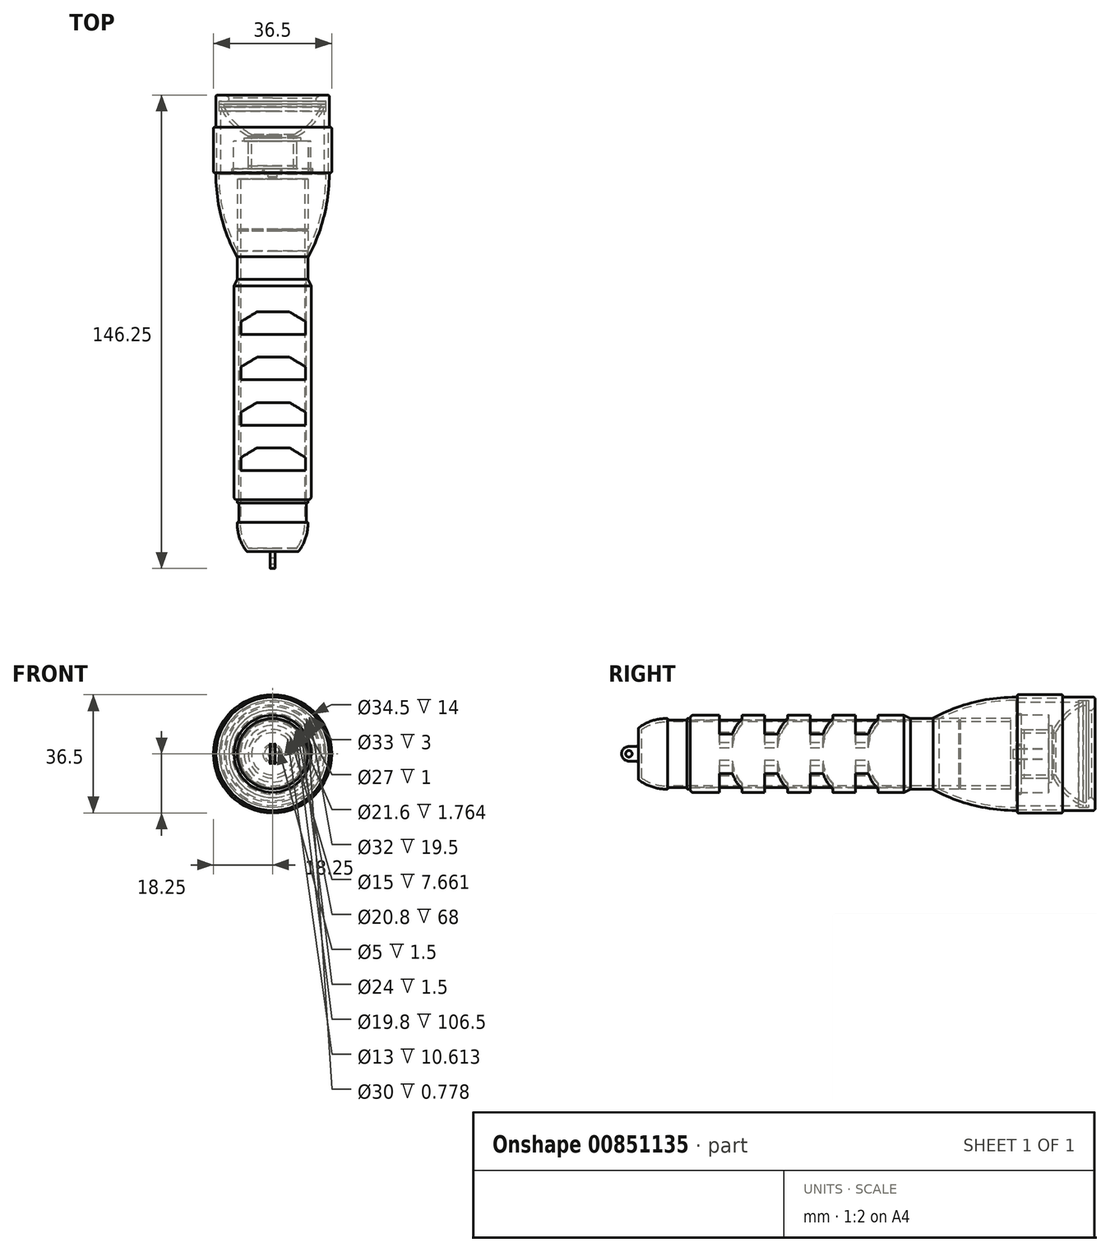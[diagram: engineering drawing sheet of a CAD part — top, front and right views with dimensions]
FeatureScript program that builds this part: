
annotation { "Feature Type Name" : "Feature", "Feature Type Description" : "" }
export const myFeature = defineFeature(function(context is Context, id is Id, definition is map)
    precondition{}
    {
        {
            var Q0;
            Q0=qCreatedBy(makeId("Right.planeOp"),FACE);
            var sketch = newSketch(context, id + "F0", { "sketchPlane" : qUnion([Q0])});
            skLineSegment(sketch, "E0", {"start": v(-10, 17.5) * mm, "end": v(0, 17.5) * mm});
            skLineSegment(sketch, "E1", {"start": v(0, 17.5) * mm, "end": v(0, 13.5) * mm});
            skLineSegment(sketch, "E2", {"start": v(0, 13.5) * mm, "end": v(-2, 13.5) * mm});
            skLineSegment(sketch, "E3", {"start": v(-2, 13.5) * mm, "end": v(-2, 16.5) * mm});
            skLineSegment(sketch, "E4", {"start": v(-2, 16.5) * mm, "end": v(-10, 16.5) * mm});
            skLineSegment(sketch, "E5", {"start": v(-10, 16.5) * mm, "end": v(-10, 17.5) * mm});
            skLineSegment(sketch, "E6", {"start": v(0, 0) * mm, "end": v(-44.18, 0) * mm, "construction": true});
            skSolve(sketch);
        }
        {
            var Q0;
            Q0 = qSketchRegion(id + "F0", true);
            var Q1;
            Q1=sQuery(id+"F0.wireOp",EDGE,"E6");
            revolve(context, id + "F1", {"surfaceOperationType" : NewSurfaceOperationType.NEW, "entities" : qUnion([Q0]), "axis" : qUnion([Q1]), "revolveType" : RevolveType.FULL});
        }
        {
            var Q0;
            Q0=makeQuery(id+"F1.opRevolve","SWEPT_EDGE",EDGE,{"disambiguationData":[OSD([sQuery(id+"F0.wireOp",EDGE,"E1"),sQuery(id+"F0.wireOp",EDGE,"E2")])]});
            chamfer(context, id + "F2", {"entities" : qUnion([Q0]), "width" : 1 * mm, "tangentPropagation" : true});
        }
        {
            var Q0;
            Q0=makeQuery(id+"F1.opRevolve","SWEPT_EDGE",EDGE,{"disambiguationData":[OSD([sQuery(id+"F0.wireOp",EDGE,"E0"),sQuery(id+"F0.wireOp",EDGE,"E1")])]});
            fillet(context, id + "F3", {"entities" : qUnion([Q0]), "radius" : .5 * mm, "tangentPropagation" : true, "allowEdgeOverflow" : false});
        }
        {
            var Q0;
            Q0=qCreatedBy(makeId("Right.planeOp"),FACE);
            var sketch = newSketch(context, id + "F4", { "sketchPlane" : qUnion([Q0])});
            skLineSegment(sketch, "E7.bottom", {"start": v(-2, 16.5) * mm, "end": v(-2.8, 16.5) * mm});
            skLineSegment(sketch, "E7.top", {"start": v(-2, 0) * mm, "end": v(-2.8, 0) * mm});
            skLineSegment(sketch, "E7.left", {"start": v(-2, 16.5) * mm, "end": v(-2, 0) * mm});
            skLineSegment(sketch, "E7.right", {"start": v(-2.8, 16.5) * mm, "end": v(-2.8, 0) * mm});
            skSolve(sketch);
        }
        {
            var Q0;
            Q0 = qSketchRegion(id + "F4", true);
            var Q1;
            Q1=sQuery(id+"F4.wireOp",EDGE,"E7.top");
            revolve(context, id + "F5", {"surfaceOperationType" : NewSurfaceOperationType.NEW, "entities" : qUnion([Q0]), "axis" : qUnion([Q1]), "revolveType" : RevolveType.FULL});
        }
        {
            var Q0;
            Q0=qCreatedBy(makeId("Right.planeOp"),FACE);
            var sketch = newSketch(context, id + "F6", { "sketchPlane" : qUnion([Q0])});
            skLineSegment(sketch, "E8", {"start": v(-22.8, 7.5) * mm, "end": v(-14.3, 7.5) * mm});
            skLineSegment(sketch, "E9", {"start": v(-22.8, 7.5) * mm, "end": v(-22.8, 6.5) * mm});
            skLineSegment(sketch, "E10", {"start": v(-22.8, 6.5) * mm, "end": v(-12.19, 6.5) * mm});
            skLineSegment(sketch, "E11", {"start": v(-3.8, 16.5) * mm, "end": v(-2.8, 16.5) * mm});
            skLineSegment(sketch, "E12", {"start": v(-2.8, 16.5) * mm, "end": v(-2.8, 15) * mm});
            skLineSegment(sketch, "E13", {"start": v(-3.8, 16.5) * mm, "end": v(-3.8, 16) * mm});
            skLineSegment(sketch, "E14", {"start": v(-3.8, 16) * mm, "end": v(2.7, 16) * mm, "construction": true});
            skArc(sketch, "E15", {"start": v(-3.8, 16) * mm, "mid": v(-9, 12.5) * mm, "end": v(-12.8, 7.5) * mm});
            skArc(sketch, "E16.0", {"start": v(-3.58, 15) * mm, "mid": v(-8.6, 11.48) * mm, "end": v(-12.19, 6.5) * mm});
            skLineSegment(sketch, "E17", {"start": v(-3.58, 15) * mm, "end": v(-2.8, 15) * mm});
            skLineSegment(sketch, "E18", {"start": v(-14.3, 7.5) * mm, "end": v(-14.3, 8.75) * mm});
            skLineSegment(sketch, "E19", {"start": v(-14.3, 8.75) * mm, "end": v(-13.3, 8.75) * mm});
            skLineSegment(sketch, "E20", {"start": v(-13.3, 8.75) * mm, "end": v(-13.3, 7.5) * mm});
            skLineSegment(sketch, "E21", {"start": v(-13.3, 7.5) * mm, "end": v(-12.8, 7.5) * mm});
            skSolve(sketch);
        }
        {
            var Q0;
            Q0 = qSketchRegion(id + "F6", true);
            var Q1;
            Q1=sQuery(id+"F0.wireOp",EDGE,"E6");
            revolve(context, id + "F7", {"surfaceOperationType" : NewSurfaceOperationType.NEW, "entities" : qUnion([Q0]), "axis" : qUnion([Q1]), "revolveType" : RevolveType.FULL});
        }
        {
            var Q0;
            Q0=qCreatedBy(makeId("Right.planeOp"),FACE);
            var sketch = newSketch(context, id + "F8", { "sketchPlane" : qUnion([Q0])});
            skLineSegment(sketch, "E22", {"start": v(-5, 16.5) * mm, "end": v(-10, 16.5) * mm});
            skLineSegment(sketch, "E23", {"start": v(-10, 16.5) * mm, "end": v(-10, 17.25) * mm});
            skLineSegment(sketch, "E24", {"start": v(-10, 17.25) * mm, "end": v(-24, 17.25) * mm});
            skLineSegment(sketch, "E25", {"start": v(-24, 17.25) * mm, "end": v(-24, 17.5) * mm});
            skLineSegment(sketch, "E26", {"start": v(-24, 17.5) * mm, "end": v(-24.5, 17.5) * mm});
            skArc(sketch, "E27", {"start": v(-24.5, 17.5) * mm, "mid": v(-37.66, 15.85) * mm, "end": v(-50, 11) * mm});
            skLineSegment(sketch, "E28", {"start": v(-5, 16.5) * mm, "end": v(-3.8, 16.5) * mm, "construction": true});
            skArc(sketch, "E29.0", {"start": v(-24.5, 16.5) * mm, "mid": v(-36.7, 15.06) * mm, "end": v(-48.24, 10.8) * mm});
            skLineSegment(sketch, "E30", {"start": v(-50, 11) * mm, "end": v(-50, 10.8) * mm});
            skLineSegment(sketch, "E31", {"start": v(-50, 10.8) * mm, "end": v(-48.24, 10.8) * mm});
            skLineSegment(sketch, "E32", {"start": v(-5, 16.5) * mm, "end": v(-5, 16) * mm});
            skLineSegment(sketch, "E33", {"start": v(-5, 16) * mm, "end": v(-24.5, 16) * mm});
            skLineSegment(sketch, "E34", {"start": v(-24.5, 16.5) * mm, "end": v(-24.5, 16) * mm});
            skSolve(sketch);
        }
        {
            var Q0;
            Q0 = qSketchRegion(id + "F8", true);
            var Q1;
            Q1=sQuery(id+"F0.wireOp",EDGE,"E6");
            revolve(context, id + "F9", {"operationType" : NewBodyOperationType.ADD, "surfaceOperationType" : NewSurfaceOperationType.NEW, "entities" : qUnion([Q0]), "axis" : qUnion([Q1]), "revolveType" : RevolveType.FULL});
        }
        {
            var Q0;
            Q0=qCreatedBy(makeId("Right.planeOp"),FACE);
            var sketch = newSketch(context, id + "F10", { "sketchPlane" : qUnion([Q0])});
            skLineSegment(sketch, "E35.bottom", {"start": v(-24, 18.25) * mm, "end": v(-10, 18.25) * mm});
            skLineSegment(sketch, "E35.top", {"start": v(-24, 17.25) * mm, "end": v(-10, 17.25) * mm});
            skLineSegment(sketch, "E35.left", {"start": v(-24, 18.25) * mm, "end": v(-24, 17.25) * mm});
            skLineSegment(sketch, "E35.right", {"start": v(-10, 18.25) * mm, "end": v(-10, 17.25) * mm});
            skSolve(sketch);
        }
        {
            var Q0;
            Q0 = qSketchRegion(id + "F10", true);
            var Q1;
            Q1=sQuery(id+"F0.wireOp",EDGE,"E6");
            revolve(context, id + "F11", {"surfaceOperationType" : NewSurfaceOperationType.NEW, "entities" : qUnion([Q0]), "axis" : qUnion([Q1]), "revolveType" : RevolveType.FULL});
        }
        {
            var Q0;
            Q0=makeQuery(id+"F11.opRevolve","SWEPT_EDGE",EDGE,{"disambiguationData":[OSD([sQuery(id+"F10.wireOp",EDGE,"E35.bottom"),sQuery(id+"F10.wireOp",EDGE,"E35.left")])]});
            var Q1;
            Q1=makeQuery(id+"F11.opRevolve","SWEPT_EDGE",EDGE,{"disambiguationData":[OSD([sQuery(id+"F10.wireOp",EDGE,"E35.bottom"),sQuery(id+"F10.wireOp",EDGE,"E35.right")])]});
            fillet(context, id + "F12", {"entities" : qUnion([Q0, Q1]), "radius" : .3 * mm, "tangentPropagation" : true, "allowEdgeOverflow" : false});
        }
        {
            var Q0;
            Q0=qCreatedBy(makeId("Right.planeOp"),FACE);
            var sketch = newSketch(context, id + "F13", { "sketchPlane" : qUnion([Q0])});
            skLineSegment(sketch, "E36", {"start": v(-41.5, 10.9) * mm, "end": v(-26, 10.9) * mm});
            skLineSegment(sketch, "E37", {"start": v(-26, 10.9) * mm, "end": v(-26, 10.4) * mm});
            skLineSegment(sketch, "E38", {"start": v(-41.5, 10.9) * mm, "end": v(-41.5, 10.4) * mm});
            skLineSegment(sketch, "E39", {"start": v(-41.5, 10.4) * mm, "end": v(-42, 10.4) * mm});
            skLineSegment(sketch, "E40", {"start": v(-42, 10.4) * mm, "end": v(-42, 10.9) * mm});
            skLineSegment(sketch, "E41", {"start": v(-42, 10.9) * mm, "end": v(-57, 10.9) * mm});
            skLineSegment(sketch, "E42", {"start": v(-57, 10.9) * mm, "end": v(-57, 10.4) * mm});
            skLineSegment(sketch, "E43", {"start": v(-125, 10.9) * mm, "end": v(-126, 10.9) * mm});
            skLineSegment(sketch, "E44", {"start": v(-126, 10.9) * mm, "end": v(-126, 10.4) * mm});
            skLineSegment(sketch, "E45", {"start": v(-235.67, 8.05) * mm, "end": v(-235.67, 10.9) * mm});
            skLineSegment(sketch, "E46", {"start": v(-141, 0) * mm, "end": v(-141, 8) * mm});
            skArc(sketch, "E47", {"start": v(-132.5, 10.9) * mm, "mid": v(-137, 10.16) * mm, "end": v(-141, 8) * mm});
            skLineSegment(sketch, "E48", {"start": v(-57, 10.4) * mm, "end": v(-125, 10.4) * mm});
            skLineSegment(sketch, "E49", {"start": v(-125, 10.4) * mm, "end": v(-125, 10.9) * mm});
            skLineSegment(sketch, "E50", {"start": v(-126, 10.4) * mm, "end": v(-132, 10.4) * mm});
            skLineSegment(sketch, "E51", {"start": v(-132, 10.4) * mm, "end": v(-132, 10.9) * mm});
            skLineSegment(sketch, "E52", {"start": v(-132, 10.9) * mm, "end": v(-132.5, 10.9) * mm});
            skLineSegment(sketch, "E53.0", {"start": v(-26, 9.9) * mm, "end": v(-132.5, 9.9) * mm});
            skLineSegment(sketch, "E54", {"start": v(-26, 9.9) * mm, "end": v(-26, 10.4) * mm});
            skArc(sketch, "E55.0", {"start": v(-132.5, 9.9) * mm, "mid": v(-136.44, 9.28) * mm, "end": v(-140, 7.5) * mm});
            skLineSegment(sketch, "E55.1", {"start": v(-140, 0) * mm, "end": v(-140, 7.5) * mm});
            skLineSegment(sketch, "E56", {"start": v(-141, 0) * mm, "end": v(-140, 0) * mm});
            skLineSegment(sketch, "E57", {"start": v(-26, 10.9) * mm, "end": v(10.32, 10.9) * mm, "construction": true});
            skLineSegment(sketch, "E58", {"start": v(0, 0) * mm, "end": v(10.28, 0) * mm});
            skLineSegment(sketch, "E59", {"start": v(-132.5, 10.9) * mm, "end": v(-141.04, 10.9) * mm, "construction": true});
            skSolve(sketch);
        }
        {
            var Q0;
            Q0=makeQuery(id+"F13.imprint","IMPRINT",FACE,{"disambiguationData":[TD([[makeQuery(id+"F13.imprint","IMPRINT",EDGE,{"derivedFrom":sQuery(id+"F13.wireOp",EDGE,"E36")}),-1.0]])]});
            var Q1;
            Q1=sQuery(id+"F13.wireOp",EDGE,"E56");
            revolve(context, id + "F14", {"surfaceOperationType" : NewSurfaceOperationType.NEW, "entities" : qUnion([Q0]), "axis" : qUnion([Q1]), "revolveType" : RevolveType.FULL});
        }
        {
            var Q0;
            Q0=qCreatedBy(makeId("Right.planeOp"),FACE);
            var sketch = newSketch(context, id + "F15", { "sketchPlane" : qUnion([Q0])});
            skLineSegment(sketch, "E60.bottom", {"start": v(-125, 10.4) * mm, "end": v(-57, 10.4) * mm});
            skLineSegment(sketch, "E60.top", {"start": v(-125, 11.9) * mm, "end": v(-57, 11.9) * mm});
            skLineSegment(sketch, "E60.left", {"start": v(-125, 10.4) * mm, "end": v(-125, 11.9) * mm});
            skLineSegment(sketch, "E60.right", {"start": v(-57, 10.4) * mm, "end": v(-57, 11.9) * mm});
            skSolve(sketch);
        }
        {
            var Q0;
            Q0 = qSketchRegion(id + "F15", true);
            var Q1;
            Q1=sQuery(id+"F0.wireOp",EDGE,"E6");
            revolve(context, id + "F16", {"surfaceOperationType" : NewSurfaceOperationType.NEW, "entities" : qUnion([Q0]), "axis" : qUnion([Q1]), "revolveType" : RevolveType.FULL});
        }
        {
            var Q0;
            Q0=qCreatedBy(makeId("Right.planeOp"),FACE);
            var sketch = newSketch(context, id + "F17", { "sketchPlane" : qUnion([Q0])});
            skCircle(sketch, "E61", {"center": v(-144, 0) * mm, "radius": 1 * mm});
            skArc(sketch, "E62", {"start": v(-144, 2.25) * mm, "mid": v(-146.25, 0) * mm, "end": v(-144, -2.25) * mm});
            skLineSegment(sketch, "E63", {"start": v(-144, 2.25) * mm, "end": v(-140.57, 2.25) * mm});
            skLineSegment(sketch, "E64", {"start": v(-140.57, 2.25) * mm, "end": v(-140.57, -2.25) * mm});
            skLineSegment(sketch, "E65", {"start": v(-140.57, -2.25) * mm, "end": v(-144, -2.25) * mm});
            skSolve(sketch);
        }
        {
            var Q0;
            Q0 = qSketchRegion(id + "F17", true);
            extrude(context, id + "F18", {"entities" : qUnion([Q0]), "operationType" : NewBodyOperationType.ADD, "endBound" : BoundingType.SYMMETRIC, "depth" : 1.5 * mm, "offsetDistance" : 25 * mm});
        }
        {
            var Q0;
            Q0=makeQuery(id+"F18.boolean.opBoolean","INTERSECT",EDGE,{"derivedFrom":[makeQuery(id+"F14.opRevolve","SWEPT_FACE",FACE,{"disambiguationData":[OSD([sQuery(id+"F13.wireOp",EDGE,"E46")])]}),makeQuery(id+"F18.opExtrude","SWEPT_FACE",FACE,{"disambiguationData":[OSD([sQuery(id+"F17.wireOp",EDGE,"E63")])]})]});
            var Q1;
            Q1=makeQuery(id+"F18.boolean.opBoolean","INTERSECT",EDGE,{"derivedFrom":[makeQuery(id+"F14.opRevolve","SWEPT_FACE",FACE,{"disambiguationData":[OSD([sQuery(id+"F13.wireOp",EDGE,"E46")])]}),makeQuery(id+"F18.opExtrude","SWEPT_FACE",FACE,{"disambiguationData":[OSD([sQuery(id+"F17.wireOp",EDGE,"E65")])]})]});
            fillet(context, id + "F19", {"entities" : qUnion([Q0, Q1]), "radius" : 1 * mm, "tangentPropagation" : true, "allowEdgeOverflow" : false});
        }
        {
            var Q0;
            Q0=makeQuery(id+"F16.opRevolve","SWEPT_EDGE",EDGE,{"disambiguationData":[OSD([sQuery(id+"F15.wireOp",EDGE,"E60.top"),sQuery(id+"F15.wireOp",EDGE,"E60.right")])]});
            chamfer(context, id + "F20", {"entities" : qUnion([Q0]), "chamferType" : ChamferType.TWO_OFFSETS, "width1" : 1 * mm, "oppositeDirection" : false, "width2" : 2 * mm, "tangentPropagation" : true});
        }
        {
            var Q0;
            Q0=makeQuery(id+"F16.opRevolve","SWEPT_EDGE",EDGE,{"disambiguationData":[OSD([sQuery(id+"F15.wireOp",EDGE,"E60.top"),sQuery(id+"F15.wireOp",EDGE,"E60.left")])]});
            fillet(context, id + "F21", {"entities" : qUnion([Q0]), "radius" : .8 * mm, "tangentPropagation" : true, "allowEdgeOverflow" : false});
        }
        {
            var Q0;
            Q0=makeQuery(id+"F14.opRevolve","SWEPT_EDGE",EDGE,{"disambiguationData":[OSD([sQuery(id+"F13.wireOp",EDGE,"E43"),sQuery(id+"F13.wireOp",EDGE,"E44")])]});
            var Q1;
            Q1=makeQuery(id+"F14.opRevolve","SWEPT_EDGE",EDGE,{"disambiguationData":[OSD([sQuery(id+"F13.wireOp",EDGE,"E51"),sQuery(id+"F13.wireOp",EDGE,"E52")])]});
            var Q2;
            Q2=makeQuery(id+"F14.opRevolve","SWEPT_EDGE",EDGE,{"disambiguationData":[OSD([sQuery(id+"F13.wireOp",EDGE,"E44"),sQuery(id+"F13.wireOp",EDGE,"E50")])]});
            var Q3;
            Q3=makeQuery(id+"F14.opRevolve","SWEPT_EDGE",EDGE,{"disambiguationData":[OSD([sQuery(id+"F13.wireOp",EDGE,"E50"),sQuery(id+"F13.wireOp",EDGE,"E51")])]});
            var Q4;
            Q4=makeQuery(id+"F18.opExtrude","CAP_EDGE",EDGE,{"disambiguationData":[OSD([sQuery(id+"F17.wireOp",EDGE,"E61")])],"isStart":false});
            var Q5;
            Q5=makeQuery(id+"F18.opExtrude","CAP_EDGE",EDGE,{"disambiguationData":[OSD([sQuery(id+"F17.wireOp",EDGE,"E63")])],"isStart":false});
            var Q6;
            Q6=makeQuery(id+"F18.opExtrude","CAP_EDGE",EDGE,{"disambiguationData":[OSD([sQuery(id+"F17.wireOp",EDGE,"E61")])],"isStart":true});
            var Q7;
            Q7=makeQuery(id+"F18.opExtrude","CAP_EDGE",EDGE,{"disambiguationData":[OSD([sQuery(id+"F17.wireOp",EDGE,"E62")])],"isStart":true});
            var Q8;
            {var subQ0=makeQuery(id+"F14.opRevolve","SWEPT_FACE",FACE,{"disambiguationData":[OSD([sQuery(id+"F13.wireOp",EDGE,"E46")])]});Q8=makeQuery(id+"F19.opFillet","BLEND_EDGE",EDGE,{"blendedFrom":[makeQuery(id+"F18.boolean.opBoolean","INTERSECT",EDGE,{"derivedFrom":[subQ0,makeQuery(id+"F18.opExtrude","SWEPT_FACE",FACE,{"disambiguationData":[OSD([sQuery(id+"F17.wireOp",EDGE,"E63")])]})]}),subQ0],"blendedInto":[subQ0]});}
            var Q9;
            Q9=makeQuery(id+"F18.boolean.opBoolean","INTERSECT",EDGE,{"derivedFrom":[makeQuery(id+"F14.opRevolve","SWEPT_FACE",FACE,{"disambiguationData":[OSD([sQuery(id+"F13.wireOp",EDGE,"E46")])]}),makeQuery(id+"F18.opExtrude","CAP_FACE",FACE,{"disambiguationData":[OSD([sQuery(id+"F17.wireOp",EDGE,"E61"),sQuery(id+"F17.wireOp",EDGE,"E62"),sQuery(id+"F17.wireOp",EDGE,"E63"),sQuery(id+"F17.wireOp",EDGE,"E64"),sQuery(id+"F17.wireOp",EDGE,"E65")])],"isStart":true})]});
            var Q10;
            Q10=makeQuery(id+"F18.boolean.opBoolean","INTERSECT",EDGE,{"derivedFrom":[makeQuery(id+"F14.opRevolve","SWEPT_FACE",FACE,{"disambiguationData":[OSD([sQuery(id+"F13.wireOp",EDGE,"E46")])]}),makeQuery(id+"F18.opExtrude","CAP_FACE",FACE,{"disambiguationData":[OSD([sQuery(id+"F17.wireOp",EDGE,"E61"),sQuery(id+"F17.wireOp",EDGE,"E62"),sQuery(id+"F17.wireOp",EDGE,"E63"),sQuery(id+"F17.wireOp",EDGE,"E64"),sQuery(id+"F17.wireOp",EDGE,"E65")])],"isStart":false})]});
            var Q11;
            {var subQ0=makeQuery(id+"F14.opRevolve","SWEPT_FACE",FACE,{"disambiguationData":[OSD([sQuery(id+"F13.wireOp",EDGE,"E46")])]});Q11=makeQuery(id+"F19.opFillet","BLEND_EDGE",EDGE,{"blendedFrom":[makeQuery(id+"F18.boolean.opBoolean","INTERSECT",EDGE,{"derivedFrom":[subQ0,makeQuery(id+"F18.opExtrude","SWEPT_FACE",FACE,{"disambiguationData":[OSD([sQuery(id+"F17.wireOp",EDGE,"E65")])]})]}),subQ0],"blendedInto":[subQ0]});}
            var Q12;
            Q12=makeQuery(id+"F14.opRevolve","SWEPT_EDGE",EDGE,{"disambiguationData":[OSD([sQuery(id+"F13.wireOp",EDGE,"E46"),sQuery(id+"F13.wireOp",EDGE,"E47")])]});
            fillet(context, id + "F22", {"entities" : qUnion([Q0, Q1, Q2, Q3, Q4, Q5, Q6, Q7, Q8, Q9, Q10, Q11, Q12]), "radius" : .15 * mm, "tangentPropagation" : true, "allowEdgeOverflow" : false});
        }
        {
            var Q0;
            Q0=qCreatedBy(makeId("Top.planeOp"),FACE);
            var sketch = newSketch(context, id + "F23", { "sketchPlane" : qUnion([Q0])});
            skLineSegment(sketch, "E66.bottom", {"start": v(-9.78, -67) * mm, "end": v(10.22, -67) * mm});
            skLineSegment(sketch, "E66.top", {"start": v(-9.78, -74) * mm, "end": v(10.22, -74) * mm});
            skLineSegment(sketch, "E66.left", {"start": v(-9.78, -67) * mm, "end": v(-9.78, -74) * mm});
            skLineSegment(sketch, "E66.right", {"start": v(10.22, -67) * mm, "end": v(10.22, -74) * mm});
            skLineSegment(sketch, "E67.bottom", {"start": v(-9.78, -81) * mm, "end": v(10.22, -81) * mm});
            skLineSegment(sketch, "E67.top", {"start": v(-9.78, -88) * mm, "end": v(10.22, -88) * mm});
            skLineSegment(sketch, "E67.left", {"start": v(-9.78, -81) * mm, "end": v(-9.78, -88) * mm});
            skLineSegment(sketch, "E67.right", {"start": v(10.22, -81) * mm, "end": v(10.22, -88) * mm});
            skLineSegment(sketch, "E68.bottom", {"start": v(-9.78, -95) * mm, "end": v(10.22, -95) * mm});
            skLineSegment(sketch, "E68.top", {"start": v(-9.78, -102) * mm, "end": v(10.22, -102) * mm});
            skLineSegment(sketch, "E68.left", {"start": v(-9.78, -95) * mm, "end": v(-9.78, -102) * mm});
            skLineSegment(sketch, "E68.right", {"start": v(10.22, -95) * mm, "end": v(10.22, -102) * mm});
            skLineSegment(sketch, "E69.bottom", {"start": v(-9.78, -109) * mm, "end": v(10.22, -109) * mm});
            skLineSegment(sketch, "E69.top", {"start": v(-9.78, -116) * mm, "end": v(10.22, -116) * mm});
            skLineSegment(sketch, "E69.left", {"start": v(-9.78, -109) * mm, "end": v(-9.78, -116) * mm});
            skLineSegment(sketch, "E69.right", {"start": v(10.22, -109) * mm, "end": v(10.22, -116) * mm});
            skLineSegment(sketch, "E70", {"start": v(0, 0) * mm, "end": v(0, -67) * mm});
            skSolve(sketch);
        }
        {
            var Q0;
            Q0 = qSketchRegion(id + "F23", true);
            extrude(context, id + "F24", {"entities" : qUnion([Q0]), "endBound" : BoundingType.SYMMETRIC, "depth" : 25 * mm, "offsetDistance" : 25 * mm});
        }
        {
            var Q0;
            Q0=makeQuery(id+"F24.opExtrude","SWEPT_EDGE",EDGE,{"disambiguationData":[OSD([sQuery(id+"F23.wireOp",EDGE,"E66.bottom"),sQuery(id+"F23.wireOp",EDGE,"E66.left")])]});
            var Q1;
            Q1=makeQuery(id+"F24.opExtrude","SWEPT_EDGE",EDGE,{"disambiguationData":[OSD([sQuery(id+"F23.wireOp",EDGE,"E67.bottom"),sQuery(id+"F23.wireOp",EDGE,"E67.left")])]});
            var Q2;
            Q2=makeQuery(id+"F24.opExtrude","SWEPT_EDGE",EDGE,{"disambiguationData":[OSD([sQuery(id+"F23.wireOp",EDGE,"E68.bottom"),sQuery(id+"F23.wireOp",EDGE,"E68.left")])]});
            var Q3;
            Q3=makeQuery(id+"F24.opExtrude","SWEPT_EDGE",EDGE,{"disambiguationData":[OSD([sQuery(id+"F23.wireOp",EDGE,"E69.bottom"),sQuery(id+"F23.wireOp",EDGE,"E69.left")])]});
            var Q4;
            Q4=makeQuery(id+"F24.opExtrude","SWEPT_EDGE",EDGE,{"disambiguationData":[OSD([sQuery(id+"F23.wireOp",EDGE,"E66.bottom"),sQuery(id+"F23.wireOp",EDGE,"E66.right")])]});
            var Q5;
            Q5=makeQuery(id+"F24.opExtrude","SWEPT_EDGE",EDGE,{"disambiguationData":[OSD([sQuery(id+"F23.wireOp",EDGE,"E67.bottom"),sQuery(id+"F23.wireOp",EDGE,"E67.right")])]});
            var Q6;
            Q6=makeQuery(id+"F24.opExtrude","SWEPT_EDGE",EDGE,{"disambiguationData":[OSD([sQuery(id+"F23.wireOp",EDGE,"E68.bottom"),sQuery(id+"F23.wireOp",EDGE,"E68.right")])]});
            var Q7;
            Q7=makeQuery(id+"F24.opExtrude","SWEPT_EDGE",EDGE,{"disambiguationData":[OSD([sQuery(id+"F23.wireOp",EDGE,"E69.bottom"),sQuery(id+"F23.wireOp",EDGE,"E69.right")])]});
            chamfer(context, id + "F25", {"entities" : qUnion([Q0, Q1, Q2, Q3, Q4, Q5, Q6, Q7]), "chamferType" : ChamferType.TWO_OFFSETS, "width1" : 3 * mm, "oppositeDirection" : false, "width2" : 5 * mm, "tangentPropagation" : true});
        }
        {
            var Q0;
            Q0=makeQuery(id+"F24.opExtrude","SWEPT_BODY",BODY,{"disambiguationData":[OSD([sQuery(id+"F23.wireOp",EDGE,"E66.bottom"),sQuery(id+"F23.wireOp",EDGE,"E66.top"),sQuery(id+"F23.wireOp",EDGE,"E66.left"),sQuery(id+"F23.wireOp",EDGE,"E66.right")])]});
            var Q1;
            Q1=makeQuery(id+"F24.opExtrude","SWEPT_BODY",BODY,{"disambiguationData":[OSD([sQuery(id+"F23.wireOp",EDGE,"E67.bottom"),sQuery(id+"F23.wireOp",EDGE,"E67.top"),sQuery(id+"F23.wireOp",EDGE,"E67.left"),sQuery(id+"F23.wireOp",EDGE,"E67.right")])]});
            var Q2;
            Q2=makeQuery(id+"F24.opExtrude","SWEPT_BODY",BODY,{"disambiguationData":[OSD([sQuery(id+"F23.wireOp",EDGE,"E68.bottom"),sQuery(id+"F23.wireOp",EDGE,"E68.top"),sQuery(id+"F23.wireOp",EDGE,"E68.left"),sQuery(id+"F23.wireOp",EDGE,"E68.right")])]});
            var Q3;
            Q3=makeQuery(id+"F24.opExtrude","SWEPT_BODY",BODY,{"disambiguationData":[OSD([sQuery(id+"F23.wireOp",EDGE,"E69.bottom"),sQuery(id+"F23.wireOp",EDGE,"E69.top"),sQuery(id+"F23.wireOp",EDGE,"E69.left"),sQuery(id+"F23.wireOp",EDGE,"E69.right")])]});
            var Q4;
            Q4=makeQuery(id+"F16.opRevolve","SWEPT_BODY",BODY,{"disambiguationData":[OSD([sQuery(id+"F15.wireOp",EDGE,"E60.bottom"),sQuery(id+"F15.wireOp",EDGE,"E60.top"),sQuery(id+"F15.wireOp",EDGE,"E60.left"),sQuery(id+"F15.wireOp",EDGE,"E60.right")])]});
            booleanBodies(context, id + "F26", {"operationType" : BooleanOperationType.SUBTRACTION, "tools" : qUnion([Q0, Q1, Q2, Q3]), "targets" : qUnion([Q4])});
        }
        {
            var Q0;
            Q0=qCreatedBy(makeId("Right.planeOp"),FACE);
            var sketch = newSketch(context, id + "F27", { "sketchPlane" : qUnion([Q0])});
            skLineSegment(sketch, "E71.bottom", {"start": v(-22.8, 2.5) * mm, "end": v(-24.3, 2.5) * mm});
            skLineSegment(sketch, "E71.top", {"start": v(-22.8, 12.5) * mm, "end": v(-24.3, 12.5) * mm});
            skLineSegment(sketch, "E71.left", {"start": v(-22.8, 2.5) * mm, "end": v(-22.8, 12.5) * mm});
            skLineSegment(sketch, "E71.right", {"start": v(-24.3, 2.5) * mm, "end": v(-24.3, 12.5) * mm});
            skSolve(sketch);
        }
        {
            var Q0;
            Q0 = qSketchRegion(id + "F27", true);
            var Q1;
            Q1=sQuery(id+"F0.wireOp",EDGE,"E6");
            revolve(context, id + "F28", {"surfaceOperationType" : NewSurfaceOperationType.NEW, "entities" : qUnion([Q0]), "axis" : qUnion([Q1]), "revolveType" : RevolveType.FULL});
        }
        {
            var Q0;
            Q0=makeQuery(id+"F28.boolean.opBoolean","SPLIT",FACE,{"disambiguationData":[TD([makeQuery(id+"F7.opRevolve","SWEPT_FACE",FACE,{"disambiguationData":[OSD([sQuery(id+"F6.wireOp",EDGE,"E8")])]})])],"derivedFrom":makeQuery(id+"F28.opRevolve","SWEPT_FACE",FACE,{"disambiguationData":[OSD([sQuery(id+"F27.wireOp",EDGE,"E71.left")])]})});
            shell(context, id + "F29", {"entities" : qUnion([Q0]), "thickness" : .5 * mm});
        }
        {
            var Q0;
            Q0=qCreatedBy(makeId("Right.planeOp"),FACE);
            var sketch = newSketch(context, id + "F30", { "sketchPlane" : qUnion([Q0])});
            skLineSegment(sketch, "E72.bottom", {"start": v(-23.8, 12) * mm, "end": v(-14.3, 12) * mm});
            skLineSegment(sketch, "E72.top", {"start": v(-21.96, 7.5) * mm, "end": v(-14.3, 7.5) * mm});
            skLineSegment(sketch, "E72.left", {"start": v(-23.8, 12) * mm, "end": v(-23.8, 7.5) * mm});
            skLineSegment(sketch, "E72.right", {"start": v(-14.3, 12) * mm, "end": v(-14.3, 7.5) * mm});
            skLineSegment(sketch, "E73", {"start": v(-23.8, 7.5) * mm, "end": v(-23.8, 1.4) * mm});
            skLineSegment(sketch, "E74", {"start": v(-25.3, 0.58) * mm, "end": v(-25.3, 0) * mm});
            skLineSegment(sketch, "E75", {"start": v(-25.3, 0) * mm, "end": v(-21.96, 0) * mm});
            skLineSegment(sketch, "E76", {"start": v(-21.96, 0) * mm, "end": v(-21.96, 7.5) * mm});
            skLineSegment(sketch, "E77", {"start": v(-23.8, 1.4) * mm, "end": v(-25.3, 1.4) * mm});
            skLineSegment(sketch, "E78", {"start": v(-25.3, 1.4) * mm, "end": v(-25.3, 0.58) * mm});
            skSolve(sketch);
        }
        {
            var Q0;
            Q0 = qSketchRegion(id + "F30", true);
            var Q1;
            Q1=sQuery(id+"F0.wireOp",EDGE,"E6");
            revolve(context, id + "F31", {"surfaceOperationType" : NewSurfaceOperationType.NEW, "entities" : qUnion([Q0]), "axis" : qUnion([Q1]), "revolveType" : RevolveType.FULL});
        }
        {
            var Q0;
            Q0=makeQuery(id+"F31.opRevolve","SWEPT_FACE",FACE,{"disambiguationData":[OSD([sQuery(id+"F30.wireOp",EDGE,"E72.right")])]});
            var sketch = newSketch(context, id + "F32", { "sketchPlane" : qUnion([Q0])});
            skLineSegment(sketch, "E79", {"start": v(-11.09, -1.56) * mm, "end": v(-11.88, -1.67) * mm});
            skLineSegment(sketch, "E80", {"start": v(-11.09, 1.56) * mm, "end": v(-11.88, 1.67) * mm});
            skArc(sketch, "E81.0", {"start": v(-11.88, 1.67) * mm, "mid": v(-12, 0) * mm, "end": v(-11.88, -1.67) * mm});
            skArc(sketch, "E82", {"start": v(-11.09, 1.56) * mm, "mid": v(-11.2, 0) * mm, "end": v(-11.09, -1.56) * mm});
            skSolve(sketch);
        }
        {
            var Q0;
            Q0 = qSketchRegion(id + "F32", true);
            extrude(context, id + "F33", {"entities" : qUnion([Q0]), "operationType" : NewBodyOperationType.REMOVE, "oppositeDirection" : true, "depth" : 25 * mm, "offsetDistance" : 25 * mm});
        }
    });
